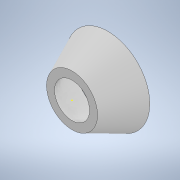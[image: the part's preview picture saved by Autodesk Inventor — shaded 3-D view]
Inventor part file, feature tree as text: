
AUTODESK INVENTOR PART (.ipt)
format: ipt  version: 2021 (Build 250183000, 183)  size: 111,616 bytes
history: native  units: in
note: dims shown in document units (in); Inventor stores cm internally (conversion verified against a paired STEP export)
features: sketch x3, extrude x2
ambient origin geometry x8: Origin, YZ Plane, XZ Plane, XY Plane, X Axis, Y Axis, Z Axis, Center Point
bodies: Solid1 (feature_tree)
feature tree (5):
  extrude  "Extrusion1"  Depth=7.0866in
  sketch  "Sketch3"  dims[d9=13.3858in d10=9.8425in d11=-0.1683in]
  extrude  "Extrusion4"  Depth=9.8425in
  sketch  "Sketch1"  dims[d0=16.5354in d1=7.0866in d2=-0.1683in]
  sketch  "Sketch5"  dims[d12=0.0344in]
